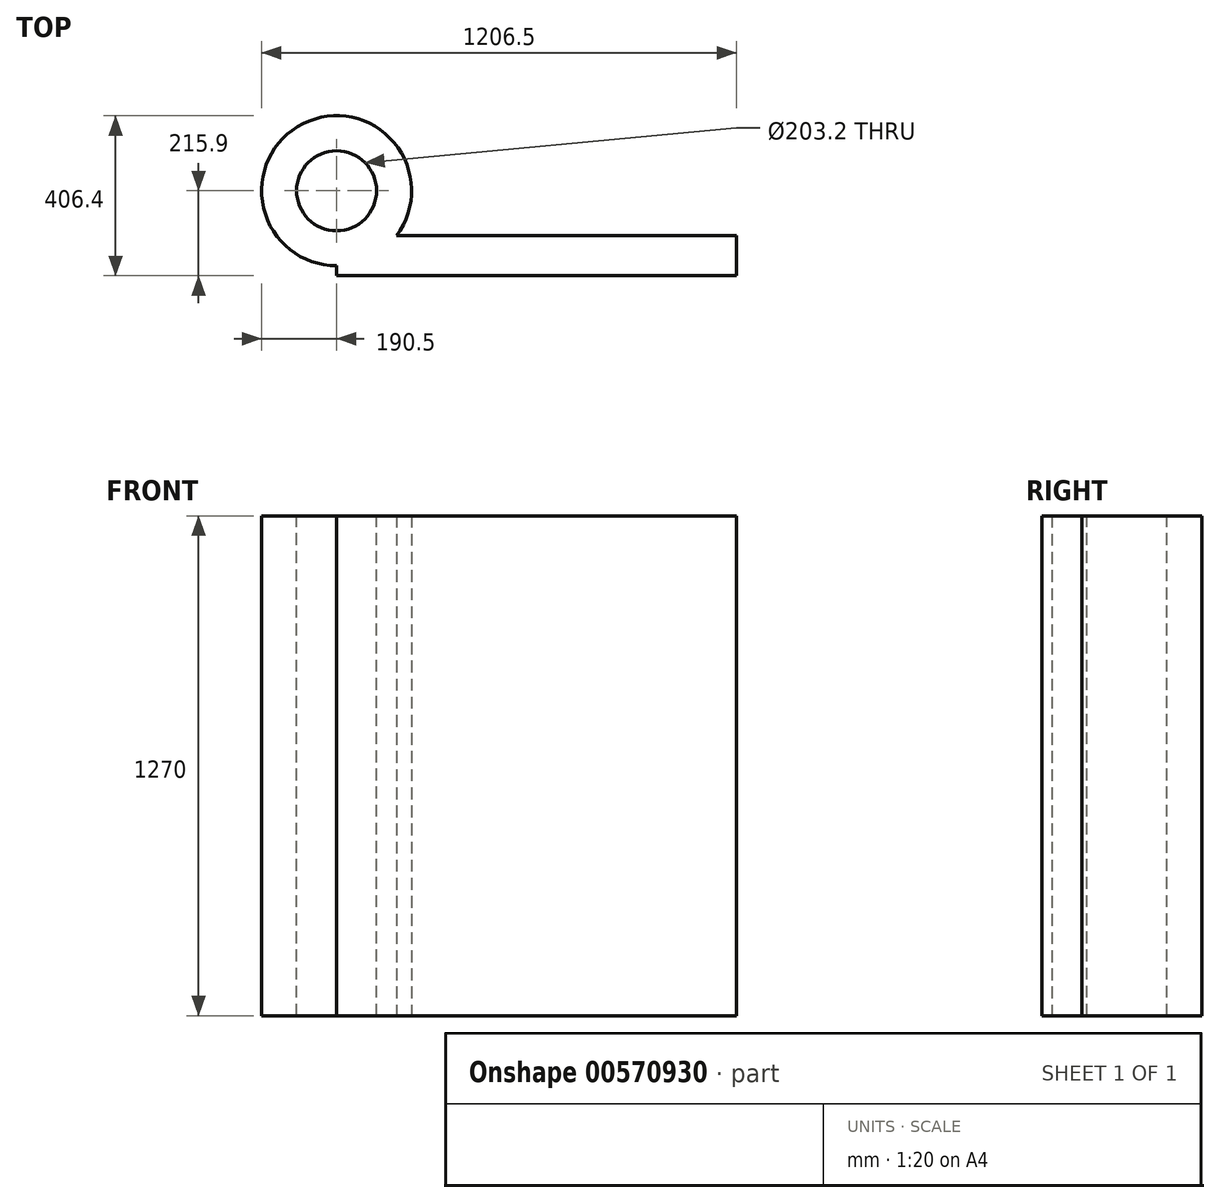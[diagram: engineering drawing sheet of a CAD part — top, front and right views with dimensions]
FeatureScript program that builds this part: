
annotation { "Feature Type Name" : "Feature", "Feature Type Description" : "" }
export const myFeature = defineFeature(function(context is Context, id is Id, definition is map)
    precondition{}
    {
        {
            var Q0;
            Q0=qCreatedBy(makeId("Top.planeOp"),FACE);
            var sketch = newSketch(context, id + "F0", { "sketchPlane" : qUnion([Q0])});
            skLineSegment(sketch, "E0", {"start": v(0, 0) * mm, "end": v(1016, 0) * mm});
            skLineSegment(sketch, "E1", {"start": v(1016, 0) * mm, "end": v(1016, 76.2) * mm});
            skLineSegment(sketch, "E2", {"start": v(1016, 76.2) * mm, "end": v(152.4, 76.2) * mm});
            skArc(sketch, "E3", {"start": v(0, 0) * mm, "mid": v(-85.2, 360.89) * mm, "end": v(152.4, 76.2) * mm});
            skSolve(sketch);
        }
        {
            var Q0;
            Q0 = qSketchRegion(id + "F0", true);
            extrude(context, id + "F1", {"entities" : qUnion([Q0]), "depth" : 1270 * mm, "offsetDistance" : 25.4 * mm});
        }
        {
            var Q0;
            Q0=makeQuery(id+"F1.opExtrude","CAP_FACE",FACE,{"disambiguationData":[OSD([sQuery(id+"F0.wireOp",EDGE,"E0"),sQuery(id+"F0.wireOp",EDGE,"E1"),sQuery(id+"F0.wireOp",EDGE,"E2"),sQuery(id+"F0.wireOp",EDGE,"E3")])],"isStart":false});
            var sketch = newSketch(context, id + "F2", { "sketchPlane" : qUnion([Q0])});
            skCircle(sketch, "E4", {"center": v(0, 190.5) * mm, "radius": 101.6 * mm});
            skSolve(sketch);
        }
        {
            var Q0;
            Q0 = qSketchRegion(id + "F2", true);
            extrude(context, id + "F3", {"entities" : qUnion([Q0]), "operationType" : NewBodyOperationType.REMOVE, "endBound" : BoundingType.THROUGH_ALL, "oppositeDirection" : true, "depth" : 25.4 * mm, "offsetDistance" : 25.4 * mm});
        }
        {
            var Q0;
            Q0=makeQuery(id+"F1.opExtrude","SWEPT_FACE",FACE,{"disambiguationData":[OSD([sQuery(id+"F0.wireOp",EDGE,"E0")])]});
            extrude(context, id + "F4", {"entities" : qUnion([Q0]), "operationType" : NewBodyOperationType.ADD, "depth" : 25.4 * mm, "offsetDistance" : 25.4 * mm});
        }
    });
